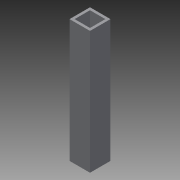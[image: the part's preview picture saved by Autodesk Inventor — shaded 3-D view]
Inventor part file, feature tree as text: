
AUTODESK INVENTOR PART (.ipt)
format: ipt  version: 2013 (Build 170138000, 138)  size: 73,216 bytes
history: native  units: in
note: dims shown in document units (in); Inventor stores cm internally (conversion verified against a paired STEP export)
features: extrude x1, sketch x1
ambient origin geometry x8: Origin, YZ Plane, XZ Plane, XY Plane, X Axis, Y Axis, Z Axis, Center Point
bodies: Solid1 (feature_tree)
feature tree (2):
  extrude  "Extrusion1"  Depth=1.0in
  sketch  "Sketch1"  dims[d0=1.0in d1=1.0in d2=0.75in d3=0.75in d4=6.0in d5=0.0in]
